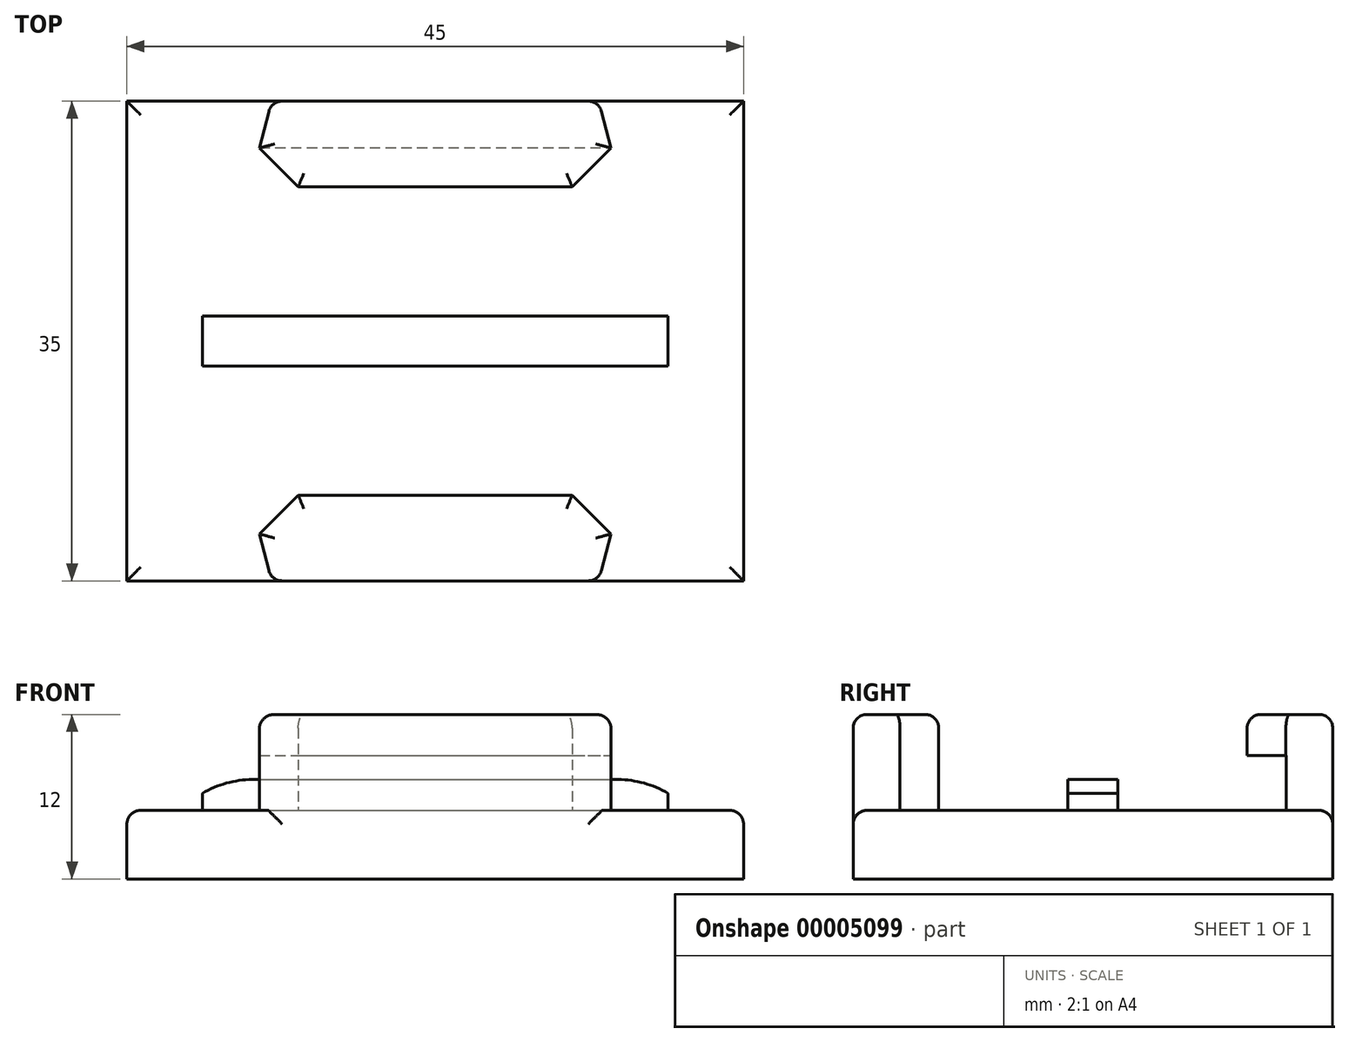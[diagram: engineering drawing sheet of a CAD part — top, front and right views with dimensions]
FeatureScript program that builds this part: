
annotation { "Feature Type Name" : "Feature", "Feature Type Description" : "" }
export const myFeature = defineFeature(function(context is Context, id is Id, definition is map)
    precondition{}
    {
        {
            var Q0;
            Q0=qCreatedBy(makeId("Top.planeOp"),FACE);
            var sketch = newSketch(context, id + "F0", { "sketchPlane" : qUnion([Q0])});
            skLineSegment(sketch, "E0.rect.bottom", {"start": v(-22.5, 17.5) * mm, "end": v(22.5, 17.5) * mm});
            skLineSegment(sketch, "E0.rect.top", {"start": v(-22.5, -17.5) * mm, "end": v(22.5, -17.5) * mm});
            skLineSegment(sketch, "E0.rect.left", {"start": v(-22.5, 17.5) * mm, "end": v(-22.5, -17.5) * mm});
            skLineSegment(sketch, "E0.rect.right", {"start": v(22.5, 17.5) * mm, "end": v(22.5, -17.5) * mm});
            skPoint(sketch, "E0.rect.middle", {"position": v(0, 0) * mm});
            skSolve(sketch);
        }
        {
            var Q0;
            Q0=makeQuery(id+"F0.imprint","IMPRINT",FACE,{"disambiguationData":[TD([[makeQuery(id+"F0.imprint","IMPRINT",EDGE,{"derivedFrom":sQuery(id+"F0.wireOp",EDGE,"E0.rect.bottom")}),-1.0]])]});
            extrude(context, id + "F1", {"entities" : qUnion([Q0]), "depth" : 5 * mm});
        }
        {
            var Q0;
            Q0=makeQuery(id+"F1.opExtrude","CAP_FACE",FACE,{"disambiguationData":[OSD([sQuery(id+"F0.wireOp",EDGE,"E0.rect.bottom"),sQuery(id+"F0.wireOp",EDGE,"E0.rect.top"),sQuery(id+"F0.wireOp",EDGE,"E0.rect.left"),sQuery(id+"F0.wireOp",EDGE,"E0.rect.right")])],"isStart":false});
            var sketch = newSketch(context, id + "F2", { "sketchPlane" : qUnion([Q0])});
            skLineSegment(sketch, "E1.rect.bottom", {"start": v(-17, 1.82) * mm, "end": v(17, 1.82) * mm});
            skLineSegment(sketch, "E1.rect.top", {"start": v(-17, -1.83) * mm, "end": v(17, -1.83) * mm});
            skLineSegment(sketch, "E1.rect.left", {"start": v(-17, 1.82) * mm, "end": v(-17, -1.83) * mm});
            skLineSegment(sketch, "E1.rect.right", {"start": v(17, 1.82) * mm, "end": v(17, -1.83) * mm});
            skPoint(sketch, "E1.rect.middle", {"position": v(0, 0) * mm});
            skSolve(sketch);
        }
        {
            var Q0;
            Q0=makeQuery(id+"F2.imprint","IMPRINT",FACE,{"disambiguationData":[TD([[makeQuery(id+"F2.imprint","IMPRINT",EDGE,{"derivedFrom":sQuery(id+"F2.wireOp",EDGE,"E1.rect.bottom")}),-1.0]])]});
            extrude(context, id + "F3", {"entities" : qUnion([Q0]), "operationType" : NewBodyOperationType.ADD, "depth" : 2.25 * mm});
        }
        {
            var Q0;
            Q0=makeQuery(id+"F3.opExtrude","SWEPT_FACE",FACE,{"disambiguationData":[OSD([sQuery(id+"F2.wireOp",EDGE,"E1.rect.top")])]});
            var sketch = newSketch(context, id + "F4", { "sketchPlane" : qUnion([Q0])});
            skLineSegment(sketch, "E2", {"start": v(-17, 7.25) * mm, "end": v(17, 7.25) * mm, "construction": true});
            skLineSegment(sketch, "E3.0", {"start": v(-17, 6.25) * mm, "end": v(17, 6.25) * mm});
            skArc(sketch, "E4", {"start": v(-13.26, 7.25) * mm, "mid": v(-15.2, 7) * mm, "end": v(-17, 6.25) * mm});
            skLineSegment(sketch, "E5", {"start": v(0, 0) * mm, "end": v(0, 15.47) * mm, "construction": true});
            skArc(sketch, "E6.0.MirrorCS", {"start": v(13.26, 7.25) * mm, "mid": v(15.2, 7) * mm, "end": v(17, 6.25) * mm});
            skLineSegment(sketch, "E7", {"start": v(-17, 6.25) * mm, "end": v(-18.16, 6.25) * mm});
            skLineSegment(sketch, "E8", {"start": v(-18.16, 6.25) * mm, "end": v(-18.16, 8.7) * mm});
            skLineSegment(sketch, "E9", {"start": v(-18.16, 8.7) * mm, "end": v(-13.25, 8.7) * mm});
            skLineSegment(sketch, "E10", {"start": v(-13.25, 8.7) * mm, "end": v(-13.26, 7.25) * mm});
            skLineSegment(sketch, "E11", {"start": v(13.26, 7.25) * mm, "end": v(13.26, 8.4) * mm});
            skLineSegment(sketch, "E12", {"start": v(13.26, 8.4) * mm, "end": v(18.11, 8.4) * mm});
            skLineSegment(sketch, "E13", {"start": v(18.11, 8.4) * mm, "end": v(18.11, 6.28) * mm});
            skLineSegment(sketch, "E14", {"start": v(18.11, 6.28) * mm, "end": v(17, 6.25) * mm});
            skSolve(sketch);
        }
        {
            var Q0;
            {var subQ0=sQuery(id+"F2.wireOp",EDGE,"E1.rect.top");var subQ1=makeQuery(id+"F3.opExtrude","CAP_EDGE",EDGE,{"disambiguationData":[OSD([subQ0])],"isStart":false});var subQ2=sQuery(id+"F4.wireOp",EDGE,"E4");var subQ3=makeQuery(id+"F4.imprint","INTERSECT",VERTEX,{"derivedFrom":[subQ1,subQ2]});var subQ6=makeQuery(id+"F4.imprint","IMPRINT",EDGE,{"disambiguationData":[TD([[subQ3,1.0]])],"derivedFrom":subQ1});var subQ8=sQuery(id+"F4.wireOp",EDGE,"E7");var subQ13=sQuery(id+"F4.wireOp",EDGE,"E6.0.MirrorCS");var subQ18=makeQuery(id+"F4.imprint","INTERSECT",VERTEX,{"derivedFrom":[subQ1,subQ13]});var subQ19=makeQuery(id+"F4.imprint","IMPRINT",EDGE,{"disambiguationData":[TD([[subQ18,-1.0]])],"derivedFrom":subQ1});var subQ20=sQuery(id+"F4.wireOp",EDGE,"E11");Q0=qUnion([makeQuery(id+"F4.imprint","IMPRINT",FACE,{"disambiguationData":[TD([[makeQuery(id+"F4.imprint","IMPRINT",EDGE,{"derivedFrom":subQ8}),-1.0]])]}),makeQuery(id+"F4.imprint","IMPRINT",FACE,{"disambiguationData":[TD([[subQ6,-1.0]])]}),makeQuery(id+"F4.imprint","IMPRINT",FACE,{"disambiguationData":[TD([[makeQuery(id+"F4.imprint","IMPRINT",EDGE,{"derivedFrom":subQ20}),-1.0]])]}),makeQuery(id+"F4.imprint","IMPRINT",FACE,{"disambiguationData":[TD([[subQ19,-1.0]])]})]);}
            extrude(context, id + "F5", {"entities" : qUnion([Q0]), "operationType" : NewBodyOperationType.REMOVE, "endBound" : BoundingType.THROUGH_ALL, "oppositeDirection" : true, "depth" : 25 * mm});
        }
        {
            var Q0;
            Q0=makeQuery(id+"F1.opExtrude","CAP_FACE",FACE,{"disambiguationData":[OSD([sQuery(id+"F0.wireOp",EDGE,"E0.rect.bottom"),sQuery(id+"F0.wireOp",EDGE,"E0.rect.top"),sQuery(id+"F0.wireOp",EDGE,"E0.rect.left"),sQuery(id+"F0.wireOp",EDGE,"E0.rect.right")])],"isStart":false});
            var sketch = newSketch(context, id + "F6", { "sketchPlane" : qUnion([Q0])});
            skLineSegment(sketch, "E15.rect.bottom", {"start": v(-11.94, 17.5) * mm, "end": v(11.94, 17.5) * mm, "construction": true});
            skPoint(sketch, "E15.rect.middle", {"position": v(0, 0) * mm});
            skLineSegment(sketch, "E16.0", {"start": v(-10, 11.25) * mm, "end": v(10, 11.25) * mm});
            skLineSegment(sketch, "E17", {"start": v(-10, 11.25) * mm, "end": v(-12.82, 14.08) * mm, "construction": true});
            skLineSegment(sketch, "E18.0.MirrorCS", {"start": v(10, 11.25) * mm, "end": v(12.82, 14.08) * mm, "construction": true});
            skLineSegment(sketch, "E19", {"start": v(10, 11.25) * mm, "end": v(12.82, 14.08) * mm});
            skLineSegment(sketch, "E20", {"start": v(11.94, 17.5) * mm, "end": v(-11.94, 17.5) * mm});
            skLineSegment(sketch, "E21", {"start": v(-12.82, 14.08) * mm, "end": v(-10, 11.25) * mm});
            skLineSegment(sketch, "E22.0.MirrorCS", {"start": v(-10, -11.25) * mm, "end": v(-12.82, -14.08) * mm, "construction": true});
            skLineSegment(sketch, "E22.1.MirrorCS", {"start": v(-11.94, -17.5) * mm, "end": v(11.94, -17.5) * mm, "construction": true});
            skLineSegment(sketch, "E22.2.MirrorCS", {"start": v(-11.94, -17.5) * mm, "end": v(11.94, -17.5) * mm, "construction": true});
            skLineSegment(sketch, "E22.4.MirrorCS", {"start": v(-10, -11.25) * mm, "end": v(-12.82, -14.08) * mm, "construction": true});
            skLineSegment(sketch, "E22.5.MirrorCS", {"start": v(10, -11.25) * mm, "end": v(12.82, -14.08) * mm, "construction": true});
            skLineSegment(sketch, "E22.7.MirrorCS", {"start": v(11.94, -17.5) * mm, "end": v(-11.94, -17.5) * mm});
            skLineSegment(sketch, "E22.9.MirrorCS", {"start": v(10, -11.25) * mm, "end": v(12.82, -14.08) * mm});
            skLineSegment(sketch, "E22.10.MirrorCS", {"start": v(-12.82, -14.08) * mm, "end": v(-10, -11.25) * mm});
            skLineSegment(sketch, "E22.12.MirrorCS", {"start": v(-10, -11.25) * mm, "end": v(10, -11.25) * mm});
            skLineSegment(sketch, "E23", {"start": v(12.82, 14.08) * mm, "end": v(11.94, 17.5) * mm});
            skLineSegment(sketch, "E24.0.MirrorCS", {"start": v(12.82, -14.08) * mm, "end": v(11.94, -17.5) * mm});
            skLineSegment(sketch, "E25.0.MirrorCS", {"start": v(-12.82, 14.08) * mm, "end": v(-11.94, 17.5) * mm});
            skLineSegment(sketch, "E26.0.MirrorCS", {"start": v(-12.82, -14.08) * mm, "end": v(-11.94, -17.5) * mm});
            skSolve(sketch);
        }
        {
            var Q0;
            {Q0=qUnion([makeQuery(id+"F6.imprint","IMPRINT",FACE,{"disambiguationData":[TD([[makeQuery(id+"F6.imprint","IMPRINT",EDGE,{"derivedFrom":sQuery(id+"F6.wireOp",EDGE,"E16.0")}),1.0]])]}),makeQuery(id+"F6.imprint","IMPRINT",FACE,{"disambiguationData":[TD([[makeQuery(id+"F6.imprint","IMPRINT",EDGE,{"derivedFrom":sQuery(id+"F6.wireOp",EDGE,"E22.7.MirrorCS")}),1.0]])]})]);}
            extrude(context, id + "F7", {"entities" : qUnion([Q0]), "operationType" : NewBodyOperationType.ADD, "depth" : 7 * mm});
        }
        {
            var Q0;
            Q0=qCreatedBy(makeId("Right.planeOp"),FACE);
            var sketch = newSketch(context, id + "F8", { "sketchPlane" : qUnion([Q0])});
            skLineSegment(sketch, "E27.0", {"start": v(14.1, 9) * mm, "end": v(14.1, 5) * mm});
            skLineSegment(sketch, "E28.bottom", {"start": v(14.1, 5) * mm, "end": v(10.15, 5) * mm});
            skLineSegment(sketch, "E28.top", {"start": v(14.1, 9) * mm, "end": v(10.15, 9) * mm});
            skLineSegment(sketch, "E28.left", {"start": v(14.1, 5) * mm, "end": v(14.1, 9) * mm});
            skLineSegment(sketch, "E28.right", {"start": v(10.15, 5) * mm, "end": v(10.15, 9) * mm});
            skLineSegment(sketch, "E29.0.MirrorCS", {"start": v(-14.1, 5) * mm, "end": v(-14.1, 9) * mm});
            skLineSegment(sketch, "E29.1.MirrorCS", {"start": v(-14.1, 9) * mm, "end": v(-14.1, 5) * mm});
            skLineSegment(sketch, "E29.2.MirrorCS", {"start": v(-14.1, 9) * mm, "end": v(-10.15, 9) * mm});
            skLineSegment(sketch, "E29.3.MirrorCS", {"start": v(-10.15, 5) * mm, "end": v(-10.15, 9) * mm});
            skLineSegment(sketch, "E29.4.MirrorCS", {"start": v(-14.1, 5) * mm, "end": v(-10.15, 5) * mm});
            skSolve(sketch);
        }
        {
            var Q0;
            {Q0=qUnion([makeQuery(id+"F8.imprint","IMPRINT",FACE,{"disambiguationData":[TD([[makeQuery(id+"F8.imprint","IMPRINT",EDGE,{"derivedFrom":sQuery(id+"F8.wireOp",EDGE,"E28.bottom")}),-1.0]])]}),makeQuery(id+"F8.imprint","IMPRINT",FACE,{"disambiguationData":[TD([[makeQuery(id+"F8.imprint","IMPRINT",EDGE,{"derivedFrom":sQuery(id+"F8.wireOp",EDGE,"E29.1.MirrorCS")}),1.0]])]})]);}
            extrude(context, id + "F9", {"entities" : qUnion([Q0]), "operationType" : NewBodyOperationType.REMOVE, "endBound" : BoundingType.SYMMETRIC, "oppositeDirection" : true, "depth" : 31.01 * mm});
        }
        {
            var Q0;
            Q0=makeQuery(id+"F7.opExtrude","CAP_FACE",FACE,{"disambiguationData":[OSD([sQuery(id+"F6.wireOp",EDGE,"E16.0"),sQuery(id+"F6.wireOp",EDGE,"E19"),sQuery(id+"F6.wireOp",EDGE,"E20"),sQuery(id+"F6.wireOp",EDGE,"E21"),sQuery(id+"F6.wireOp",EDGE,"E23"),sQuery(id+"F6.wireOp",EDGE,"E25.0.MirrorCS")])],"isStart":false});
            var Q1;
            Q1=makeQuery(id+"F7.opExtrude","CAP_FACE",FACE,{"disambiguationData":[OSD([sQuery(id+"F6.wireOp",EDGE,"E22.7.MirrorCS"),sQuery(id+"F6.wireOp",EDGE,"E22.9.MirrorCS"),sQuery(id+"F6.wireOp",EDGE,"E22.10.MirrorCS"),sQuery(id+"F6.wireOp",EDGE,"E22.12.MirrorCS"),sQuery(id+"F6.wireOp",EDGE,"E24.0.MirrorCS"),sQuery(id+"F6.wireOp",EDGE,"E26.0.MirrorCS")])],"isStart":false});
            var Q2;
            Q2=makeQuery(id+"F7.opExtrude","SWEPT_EDGE",EDGE,{"disambiguationData":[OSD([sQuery(id+"F0.wireOp",EDGE,"E0.rect.bottom"),sQuery(id+"F6.wireOp",EDGE,"E20"),sQuery(id+"F6.wireOp",EDGE,"E23")])]});
            var Q3;
            Q3=makeQuery(id+"F7.opExtrude","SWEPT_EDGE",EDGE,{"disambiguationData":[OSD([sQuery(id+"F0.wireOp",EDGE,"E0.rect.bottom"),sQuery(id+"F6.wireOp",EDGE,"E20"),sQuery(id+"F6.wireOp",EDGE,"E25.0.MirrorCS")])]});
            var Q4;
            Q4=makeQuery(id+"F7.opExtrude","SWEPT_EDGE",EDGE,{"disambiguationData":[OSD([sQuery(id+"F0.wireOp",EDGE,"E0.rect.top"),sQuery(id+"F6.wireOp",EDGE,"E22.7.MirrorCS"),sQuery(id+"F6.wireOp",EDGE,"E24.0.MirrorCS")])]});
            var Q5;
            Q5=makeQuery(id+"F7.opExtrude","SWEPT_EDGE",EDGE,{"disambiguationData":[OSD([sQuery(id+"F0.wireOp",EDGE,"E0.rect.top"),sQuery(id+"F6.wireOp",EDGE,"E22.7.MirrorCS"),sQuery(id+"F6.wireOp",EDGE,"E26.0.MirrorCS")])]});
            fillet(context, id + "F10", {"entities" : qUnion([Q0, Q1, Q2, Q3, Q4, Q5]), "radius" : 1 * mm, "tangentPropagation" : true, "allowEdgeOverflow" : false});
        }
        {
            var Q0;
            {var subQ0=sQuery(id+"F0.wireOp",EDGE,"E0.rect.top");var subQ1=sQuery(id+"F0.wireOp",EDGE,"E0.rect.right");Q0=makeQuery(id+"F7.boolean.opBoolean","SPLIT",EDGE,{"disambiguationData":[TD([makeQuery(id+"F1.opExtrude","SWEPT_FACE",FACE,{"disambiguationData":[OSD([subQ1])]})])],"derivedFrom":makeQuery(id+"F1.opExtrude","CAP_EDGE",EDGE,{"disambiguationData":[OSD([subQ0])],"isStart":false})});}
            var Q1;
            Q1=makeQuery(id+"F1.opExtrude","CAP_EDGE",EDGE,{"disambiguationData":[OSD([sQuery(id+"F0.wireOp",EDGE,"E0.rect.right")])],"isStart":false});
            var Q2;
            {var subQ0=sQuery(id+"F0.wireOp",EDGE,"E0.rect.bottom");var subQ1=sQuery(id+"F0.wireOp",EDGE,"E0.rect.right");Q2=makeQuery(id+"F7.boolean.opBoolean","SPLIT",EDGE,{"disambiguationData":[TD([makeQuery(id+"F1.opExtrude","SWEPT_FACE",FACE,{"disambiguationData":[OSD([subQ1])]})])],"derivedFrom":makeQuery(id+"F1.opExtrude","CAP_EDGE",EDGE,{"disambiguationData":[OSD([subQ0])],"isStart":false})});}
            var Q3;
            {var subQ0=sQuery(id+"F0.wireOp",EDGE,"E0.rect.bottom");var subQ1=sQuery(id+"F0.wireOp",EDGE,"E0.rect.left");Q3=makeQuery(id+"F7.boolean.opBoolean","SPLIT",EDGE,{"disambiguationData":[TD([makeQuery(id+"F1.opExtrude","SWEPT_FACE",FACE,{"disambiguationData":[OSD([subQ1])]})])],"derivedFrom":makeQuery(id+"F1.opExtrude","CAP_EDGE",EDGE,{"disambiguationData":[OSD([subQ0])],"isStart":false})});}
            var Q4;
            Q4=makeQuery(id+"F1.opExtrude","CAP_EDGE",EDGE,{"disambiguationData":[OSD([sQuery(id+"F0.wireOp",EDGE,"E0.rect.left")])],"isStart":false});
            var Q5;
            {var subQ0=sQuery(id+"F0.wireOp",EDGE,"E0.rect.top");var subQ1=sQuery(id+"F0.wireOp",EDGE,"E0.rect.left");Q5=makeQuery(id+"F7.boolean.opBoolean","SPLIT",EDGE,{"disambiguationData":[TD([makeQuery(id+"F1.opExtrude","SWEPT_FACE",FACE,{"disambiguationData":[OSD([subQ1])]})])],"derivedFrom":makeQuery(id+"F1.opExtrude","CAP_EDGE",EDGE,{"disambiguationData":[OSD([subQ0])],"isStart":false})});}
            fillet(context, id + "F11", {"entities" : qUnion([Q0, Q1, Q2, Q3, Q4, Q5]), "radius" : 1 * mm, "allowEdgeOverflow" : false});
        }
    });
